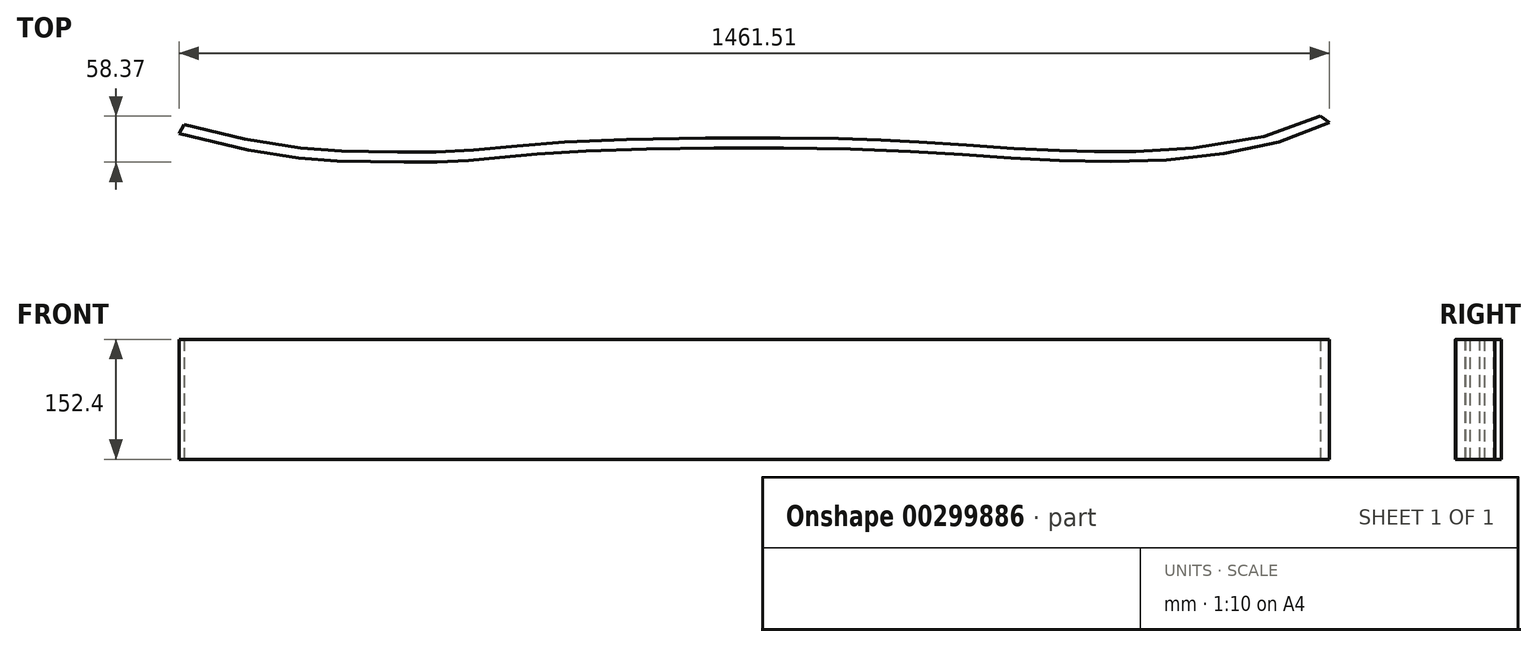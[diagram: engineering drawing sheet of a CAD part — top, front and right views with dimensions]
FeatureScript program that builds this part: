
annotation { "Feature Type Name" : "Feature", "Feature Type Description" : "" }
export const myFeature = defineFeature(function(context is Context, id is Id, definition is map)
    precondition{}
    {
        {
            var Q0;
            Q0=qCreatedBy(makeId("Top.planeOp"),FACE);
            var sketch = newSketch(context, id + "F0", { "sketchPlane" : qUnion([Q0])});
            skFitSpline(sketch, "E0", {"points": [v(-350.28, 35.64) * mm, v(-110.19, 0) * mm, v(0, 0) * mm, v(126.35, 10.84) * mm, v(542.2, 14.48) * mm, v(804.96, 0) * mm, v(1111.23, 49.23) * mm], "startDerivative": vector(2371.48, -628.44) * mm, "endDerivative": vector(1370.15, 682.34) * mm});
            skFitSpline(sketch, "E1.0", {"points": [v(-347.02, 47.92) * mm, v(-322.47, 41.41) * mm, v(-279.05, 30.86) * mm, v(-236.3, 22.64) * mm, v(-207.39, 18.33) * mm, v(-187.92, 16.04) * mm, v(-170.22, 14.53) * mm, v(-153.87, 13.61) * mm, v(-140.99, 13.2) * mm, v(-130.9, 12.99) * mm, v(-123.4, 12.87) * mm, v(-117.14, 12.8) * mm, v(-112.12, 12.73) * mm, v(-107.07, 12.66) * mm, v(-100.74, 12.56) * mm, v(-93.11, 12.43) * mm, v(-85.47, 12.3) * mm, v(-75.28, 12.12) * mm, v(-62.56, 11.93) * mm, v(-47.43, 11.8) * mm, v(-32.5, 11.8) * mm, v(-17.9, 12.02) * mm, v(-3.69, 12.48) * mm, v(10, 13.26) * mm, v(23.58, 14.32) * mm, v(37.43, 15.61) * mm, v(56.73, 17.55) * mm, v(78, 19.72) * mm, v(102.57, 21.86) * mm, v(123, 23.4) * mm, v(145.78, 24.78) * mm, v(178.94, 26.44) * mm, v(224.94, 28.13) * mm, v(285.26, 29.5) * mm, v(348.52, 30.2) * mm, v(401.85, 30.16) * mm, v(443.78, 29.74) * mm, v(474.6, 29.23) * mm, v(499.52, 28.63) * mm, v(518.86, 28.05) * mm, v(533.04, 27.56) * mm, v(546.86, 27.01) * mm, v(560.28, 26.41) * mm, v(573.34, 25.77) * mm, v(590.32, 24.86) * mm, v(610.77, 23.63) * mm, v(634.3, 22.08) * mm, v(657.03, 20.49) * mm, v(679.19, 18.91) * mm, v(700.98, 17.4) * mm, v(722.64, 16) * mm, v(744.37, 14.78) * mm, v(762.75, 13.92) * mm, v(777.71, 13.37) * mm, v(789.1, 13.03) * mm, v(800.68, 12.76) * mm, v(812.48, 12.58) * mm, v(824.5, 12.49) * mm, v(840.77, 12.5) * mm, v(861.52, 12.8) * mm, v(886.9, 13.72) * mm, v(921.13, 15.77) * mm, v(964.17, 20.14) * mm, v(1014.73, 28.94) * mm, v(1062.68, 41.93) * mm, v(1091.89, 53.79) * mm, v(1105.56, 60.6) * mm]});
            skLineSegment(sketch, "E2", {"start": v(-350.28, 35.64) * mm, "end": v(-343.75, 47.05) * mm});
            skLineSegment(sketch, "E3", {"start": v(1111.23, 49.23) * mm, "end": v(1099.32, 57.58) * mm});
            skSolve(sketch);
        }
        {
            var Q0;
            Q0 = qSketchRegion(id + "F0", true);
            var Q1;
            Q1=makeQuery(id+"F0.imprint","IMPRINT",FACE,{"disambiguationData":[TD([[makeQuery(id+"F0.imprint","IMPRINT",EDGE,{"derivedFrom":sQuery(id+"F0.wireOp",EDGE,"E0")}),1.0]])]});
            extrude(context, id + "F1", {"entities" : qUnion([Q0, Q1]), "endBound" : BoundingType.SYMMETRIC, "depth" : 152.4 * mm});
        }
    });
